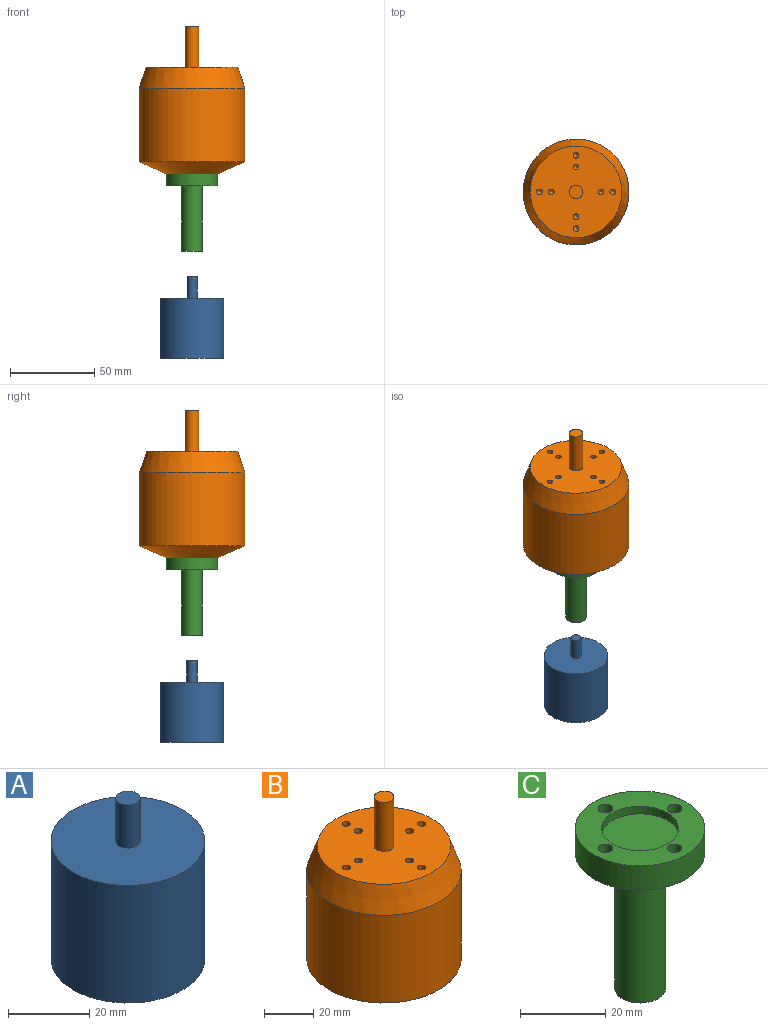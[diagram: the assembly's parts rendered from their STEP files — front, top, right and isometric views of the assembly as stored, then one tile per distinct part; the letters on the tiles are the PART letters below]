
ASSEMBLY  parts=3 mates=2
PART A: 5 faces, bbox 38x38x48.5 mm
  f0: plane 38x38mm, normal (0,0,-1), area 1134.1mm2, adj f1
  f1: cylinder r=19mm len=38mm, axis (0,0,-1), area 4238mm2, adj f0,f2
  f2: plane 38x38mm, normal (0,0,1), area 1105.8mm2, adj f1,f3
  f3: cylinder r=3mm len=13mm, axis (0,0,-1), area 245mm2, adj f2,f4
  f4: plane 6x6mm, normal (0,0,1), area 28.3mm2, adj f3
PART B: 33 faces, bbox 63x63x90 mm
  f0: plane 18x18mm, normal (0,0,-1), area 254.5mm2, adj f1
  f1: cylinder r=9mm len=18mm, axis (0,0,-1), area 113.1mm2, adj f0,f2
  f2: plane 30.5x30.5mm, normal (0,0,-1), area 456.5mm2, adj f1,f3,f25,f27,f29,f31
  f3: cone r=15.25mm half-angle=66.1deg, axis (0,0,1), area 2610.4mm2, adj f2,f4
  f4: cylinder r=31.5mm len=63mm, axis (0,0,-1), area 8668.9mm2, adj f3,f5
  f5: cone r=27.25mm half-angle=18.8deg, axis (0,0,-1), area 2436.8mm2, adj f4,f6
  f6: plane 54.5x54.5mm, normal (0,0,1), area 2214.1mm2, adj f5,f7,f9,f11,f13,f15,f17,f19
  f7: cylinder r=4mm len=24.5mm, axis (0,0,-1), area 615.8mm2, adj f6,f8
  f8: plane 8x8mm, normal (0,0,1), area 50.3mm2, adj f7
  f9: cylinder r=1.65mm len=14.1mm, axis (0,0,1), area 146.2mm2, adj f6,f10
  f10: cone r=0mm half-angle=59deg, axis (0,0,1), area 10mm2, adj f9
  f11: cylinder r=1.65mm len=14.1mm, axis (0,0,1), area 146.2mm2, adj f6,f12
  f12: cone r=0mm half-angle=59deg, axis (0,0,1), area 10mm2, adj f11
  f13: cylinder r=1.65mm len=14.1mm, axis (0,0,1), area 146.2mm2, adj f6,f14
  f14: cone r=0mm half-angle=59deg, axis (0,0,1), area 10mm2, adj f13
  f15: cylinder r=1.65mm len=14.1mm, axis (0,0,1), area 146.2mm2, adj f6,f16
  f16: cone r=0mm half-angle=59deg, axis (0,0,1), area 10mm2, adj f15
  f17: cylinder r=1.65mm len=14.1mm, axis (0,0,1), area 146.2mm2, adj f6,f18
  f18: cone r=0mm half-angle=59deg, axis (0,0,1), area 10mm2, adj f17
  f19: cylinder r=1.65mm len=14.1mm, axis (0,0,1), area 146.2mm2, adj f6,f20
  f20: cone r=0mm half-angle=59deg, axis (0,0,1), area 10mm2, adj f19
  f21: cylinder r=1.65mm len=14.1mm, axis (0,0,1), area 146.2mm2, adj f6,f22
  f22: cone r=0mm half-angle=59deg, axis (0,0,1), area 10mm2, adj f21
  f23: cylinder r=1.65mm len=14.1mm, axis (0,0,1), area 146.2mm2, adj f6,f24
  f24: cone r=0mm half-angle=59deg, axis (0,0,1), area 10mm2, adj f23
  f25: cylinder r=1.25mm len=13.5mm, axis (0,0,-1), area 106mm2, adj f2,f26
  f26: cone r=0mm half-angle=59deg, axis (0,0,-1), area 5.7mm2, adj f25
  f27: cylinder r=1.25mm len=13.5mm, axis (0,0,-1), area 106mm2, adj f2,f28
  f28: cone r=0mm half-angle=59deg, axis (0,0,-1), area 5.7mm2, adj f27
  f29: cylinder r=1.25mm len=13.5mm, axis (0,0,-1), area 106mm2, adj f2,f30
  f30: cone r=0mm half-angle=59deg, axis (0,0,-1), area 5.7mm2, adj f29
  f31: cylinder r=1.25mm len=13.5mm, axis (0,0,-1), area 106mm2, adj f2,f32
  f32: cone r=0mm half-angle=59deg, axis (0,0,-1), area 5.7mm2, adj f31
PART C: 19 faces, bbox 30.5x30.5x46 mm
  f0: cylinder r=1.7mm len=3.45mm, axis (0,0,-1), area 36.9mm2, adj f7,f18
  f1: cylinder r=1.7mm len=3.45mm, axis (0,0,-1), area 36.9mm2, adj f7,f17
  f2: cylinder r=1.7mm len=3.45mm, axis (0,0,-1), area 36.9mm2, adj f7,f16
  f3: cylinder r=1.7mm len=3.45mm, axis (0,0,-1), area 36.9mm2, adj f7,f15
  f4: cylinder r=6mm len=39mm, axis (0,0,1), area 1470.3mm2, adj f5,f10
  f5: plane 30.5x30.5mm, normal (0,0,-1), area 484.9mm2, adj f4,f6,f11,f12,f13,f14
  f6: cylinder r=15.25mm len=30.5mm, axis (0,0,1), area 670.7mm2, adj f5,f7
  f7: plane 30.5x30.5mm, normal (0,0,1), area 437.6mm2, adj f0,f1,f2,f3,f6,f8
  f8: cylinder r=9.04mm len=18.08mm, axis (0,0,1), area 125mm2, adj f7,f9
  f9: plane 18.08x18.08mm, normal (0,0,1), area 256.7mm2, adj f8
  f10: plane 12x12mm, normal (0,0,-1), area 113.1mm2, adj f4
  f11: cylinder r=3.25mm len=6.5mm, axis (0,0,-1), area 40.8mm2, adj f5,f18
  f12: cylinder r=3.25mm len=6.5mm, axis (0,0,-1), area 40.8mm2, adj f5,f17
  f13: cylinder r=3.25mm len=6.5mm, axis (0,0,-1), area 40.8mm2, adj f5,f16
  f14: cylinder r=3.25mm len=6.5mm, axis (0,0,-1), area 40.8mm2, adj f5,f15
  f15: cone r=1.7mm half-angle=45deg, axis (0,0,-1), area 34.1mm2, adj f3,f14
  f16: cone r=1.7mm half-angle=45deg, axis (0,0,-1), area 34.1mm2, adj f2,f13
  f17: cone r=1.7mm half-angle=45deg, axis (0,0,-1), area 34.1mm2, adj f1,f12
  f18: cone r=1.7mm half-angle=45deg, axis (0,0,-1), area 34.1mm2, adj f0,f11
PLACE A rot(axis=(0,0,1),128.4deg) t=(-93.14,117.58,-107.5)mm
PLACE B at identity fixed
PLACE C at identity
MATE fastened C.f4 <-> B.f3  axis (0,0,1) through (0,0,2)mm
MATE cylindrical A.f3 <-> C.f4  axis (0,0,-1) through (0,0,-59)mm
